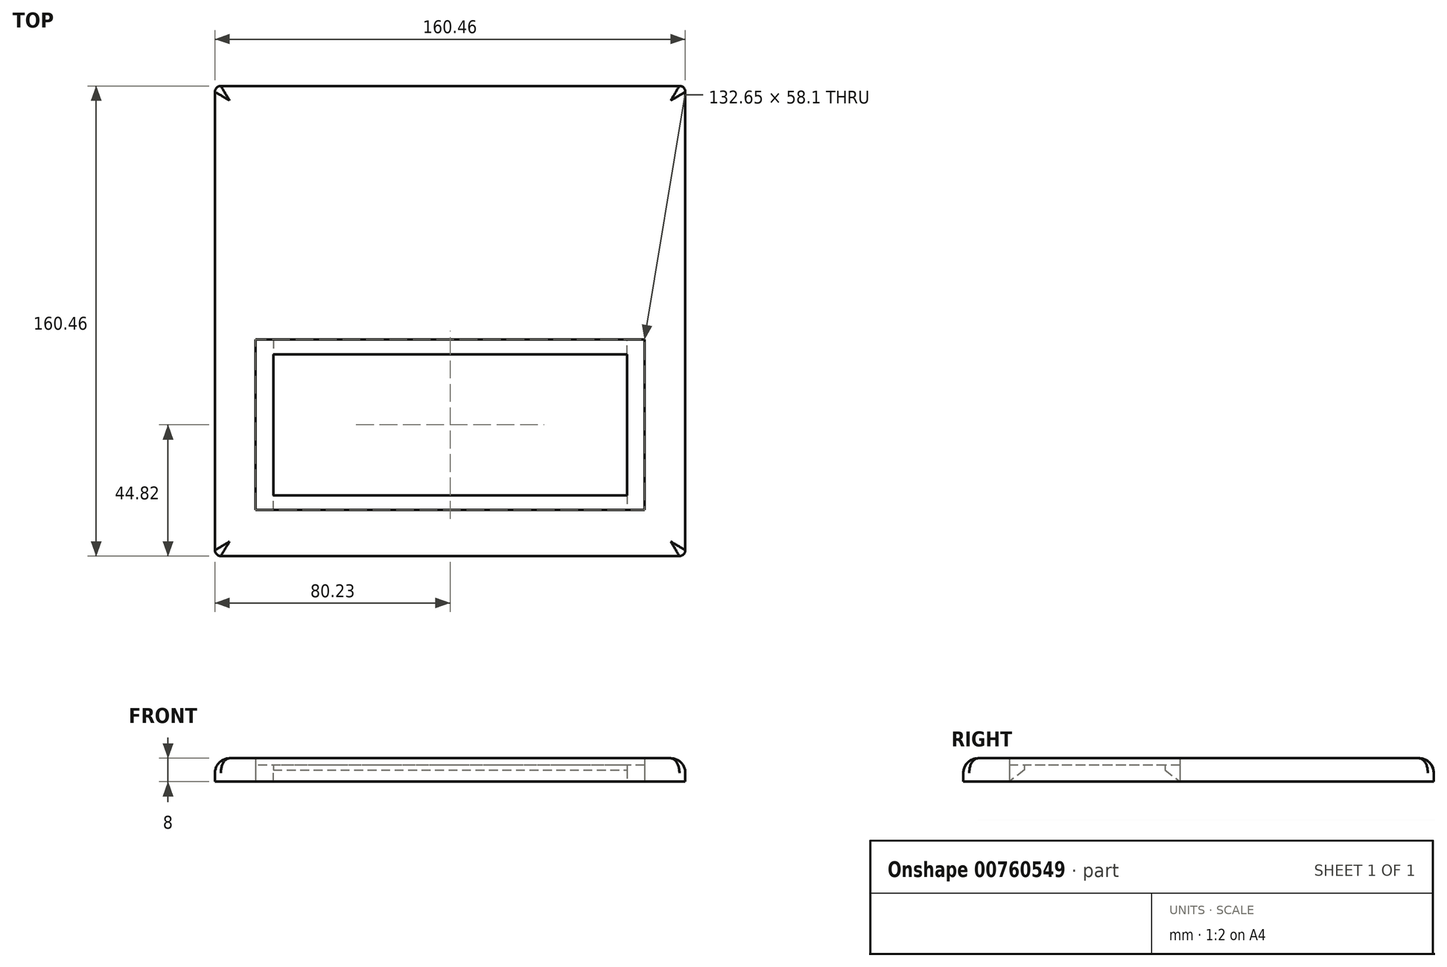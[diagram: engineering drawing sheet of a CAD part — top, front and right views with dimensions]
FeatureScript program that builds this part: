
annotation { "Feature Type Name" : "Feature", "Feature Type Description" : "" }
export const myFeature = defineFeature(function(context is Context, id is Id, definition is map)
    precondition{}
    {
        {
            var Q0;
            Q0=qCreatedBy(makeId("Top.planeOp"),FACE);
            var sketch = newSketch(context, id + "F0", { "sketchPlane" : qUnion([Q0])});
            skLineSegment(sketch, "E0.bottom", {"start": v(-78.23, 80.23) * mm, "end": v(78.23, 80.23) * mm});
            skLineSegment(sketch, "E0.top", {"start": v(-78.23, -80.23) * mm, "end": v(78.23, -80.23) * mm});
            skLineSegment(sketch, "E0.left", {"start": v(-80.23, 78.23) * mm, "end": v(-80.23, -78.23) * mm});
            skLineSegment(sketch, "E0.right", {"start": v(80.23, 78.23) * mm, "end": v(80.23, -78.23) * mm});
            skPoint(sketch, "E0.middle", {"position": v(0, 0) * mm});
            skPoint(sketch, "E1.visualSharp", {"position": v(-80.23, 80.23) * mm});
            skArc(sketch, "E1.filletArc", {"start": v(-78.23, 80.23) * mm, "mid": v(-79.65, 79.65) * mm, "end": v(-80.23, 78.23) * mm});
            skPoint(sketch, "E2.visualSharp", {"position": v(80.23, -80.23) * mm});
            skArc(sketch, "E2.filletArc", {"start": v(78.23, -80.23) * mm, "mid": v(79.65, -79.65) * mm, "end": v(80.23, -78.23) * mm});
            skPoint(sketch, "E3.visualSharp", {"position": v(80.23, 80.23) * mm});
            skArc(sketch, "E3.filletArc", {"start": v(80.23, 78.23) * mm, "mid": v(79.65, 79.65) * mm, "end": v(78.23, 80.23) * mm});
            skPoint(sketch, "E4.visualSharp", {"position": v(-80.23, -80.23) * mm});
            skArc(sketch, "E4.filletArc", {"start": v(-80.23, -78.23) * mm, "mid": v(-79.65, -79.65) * mm, "end": v(-78.23, -80.23) * mm});
            skLineSegment(sketch, "E5.bottom", {"start": v(66.33, -6.36) * mm, "end": v(-66.33, -6.36) * mm});
            skLineSegment(sketch, "E5.top", {"start": v(66.33, -64.46) * mm, "end": v(-66.33, -64.46) * mm});
            skLineSegment(sketch, "E5.left", {"start": v(66.33, -6.36) * mm, "end": v(66.33, -64.46) * mm});
            skLineSegment(sketch, "E5.right", {"start": v(-66.33, -6.36) * mm, "end": v(-66.33, -64.46) * mm});
            skPoint(sketch, "E5.middle", {"position": v(0, -35.4) * mm});
            skLineSegment(sketch, "E6.bottom", {"start": v(60.33, -11.36) * mm, "end": v(-60.33, -11.36) * mm});
            skLineSegment(sketch, "E6.top", {"start": v(60.33, -59.46) * mm, "end": v(-60.33, -59.46) * mm});
            skLineSegment(sketch, "E6.left", {"start": v(60.33, -11.36) * mm, "end": v(60.33, -59.46) * mm});
            skLineSegment(sketch, "E6.right", {"start": v(-60.33, -11.36) * mm, "end": v(-60.33, -59.46) * mm});
            skSolve(sketch);
        }
        {
            var Q0;
            Q0 = qSketchRegion(id + "F0", true);
            extrude(context, id + "F1", {"entities" : qUnion([Q0]), "depth" : 8 * mm, "offsetDistance" : 25 * mm});
        }
        {
            var Q0;
            Q0=makeQuery(id+"F1.opExtrude","CAP_EDGE",EDGE,{"disambiguationData":[OSD([sQuery(id+"F0.wireOp",EDGE,"E0.top")])],"isStart":false});
            fillet(context, id + "F2", {"entities" : qUnion([Q0]), "radius" : 5 * mm, "tangentPropagation" : true, "allowEdgeOverflow" : false});
        }
        {
            var Q0;
            Q0=makeQuery(id+"F0.imprint","IMPRINT",FACE,{"disambiguationData":[TD([[makeQuery(id+"F0.imprint","IMPRINT",EDGE,{"derivedFrom":sQuery(id+"F0.wireOp",EDGE,"E5.bottom")}),1.0]])]});
            extrude(context, id + "F3", {"entities" : qUnion([Q0]), "depth" : (8 - 2.38) * mm, "offsetDistance" : 25 * mm});
        }
        {
            var Q0;
            Q0=makeQuery(id+"F3.opExtrude","CAP_EDGE",EDGE,{"disambiguationData":[OSD([sQuery(id+"F0.wireOp",EDGE,"E6.bottom")])],"isStart":true});
            var Q1;
            Q1=makeQuery(id+"F3.opExtrude","CAP_EDGE",EDGE,{"disambiguationData":[OSD([sQuery(id+"F0.wireOp",EDGE,"E6.top")])],"isStart":true});
            chamfer(context, id + "F4", {"entities" : qUnion([Q0, Q1]), "chamferType" : ChamferType.TWO_OFFSETS, "width1" : 5 * mm, "oppositeDirection" : false, "width2" : 4 * mm, "tangentPropagation" : true});
        }
    });
